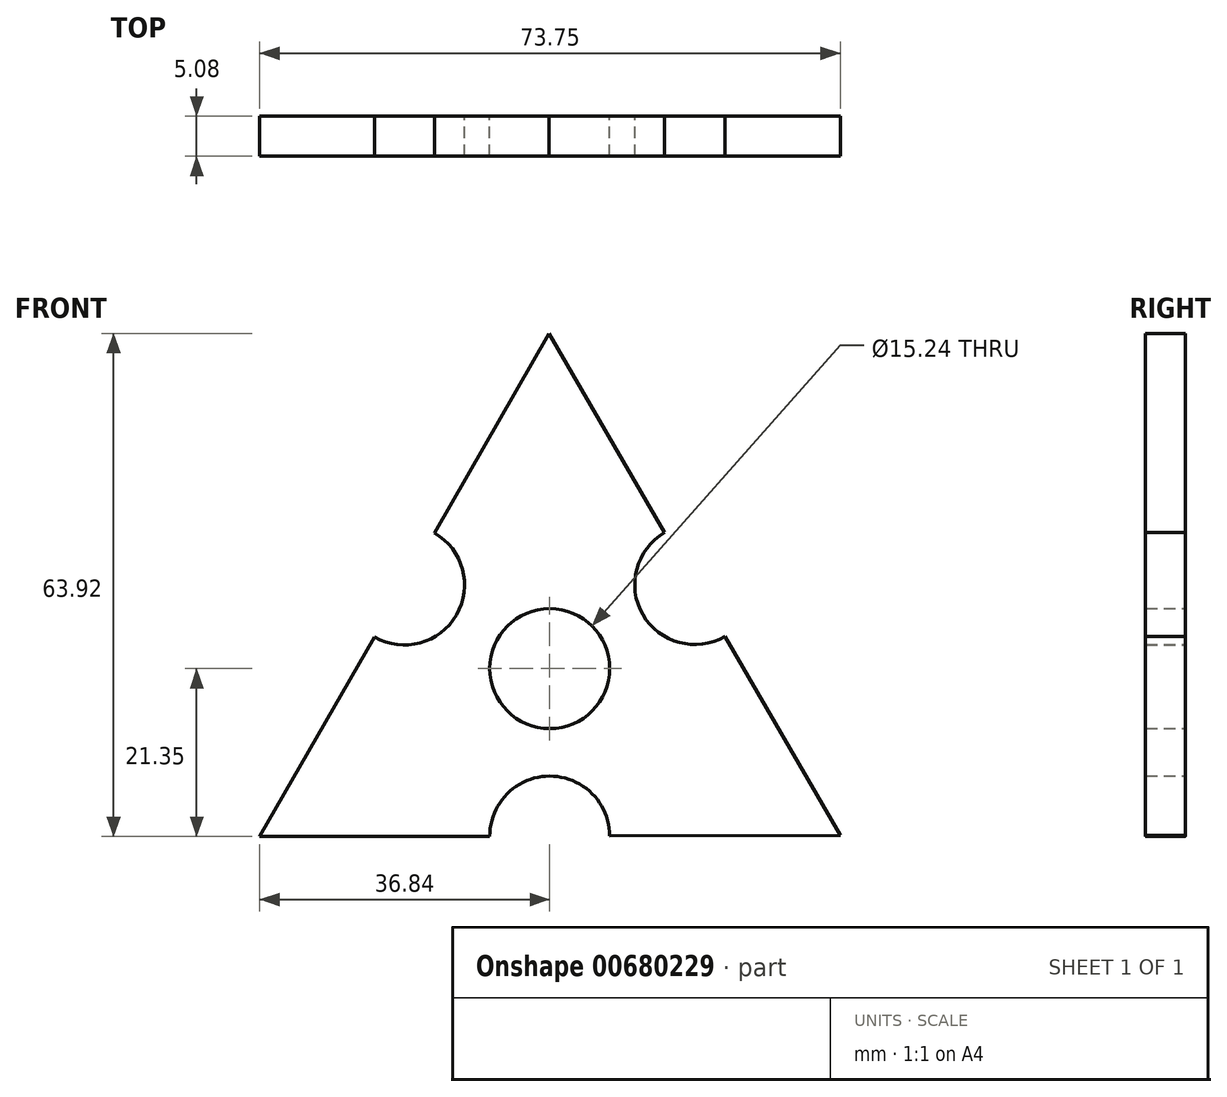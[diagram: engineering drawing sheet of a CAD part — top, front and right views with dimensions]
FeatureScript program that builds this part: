
annotation { "Feature Type Name" : "Feature", "Feature Type Description" : "" }
export const myFeature = defineFeature(function(context is Context, id is Id, definition is map)
    precondition{}
    {
        {
            var Q0;
            Q0=qCreatedBy(makeId("Front.planeOp"),FACE);
            var sketch = newSketch(context, id + "F0", { "sketchPlane" : qUnion([Q0])});
            skCircle(sketch, "E0.cCircle", {"center": v(0, 0) * mm, "radius": 36.87 * mm, "construction": true});
            skLineSegment(sketch, "E0.0", {"start": v(36.9, -21.23) * mm, "end": v(0.07, -42.57) * mm});
            skLineSegment(sketch, "E0.1", {"start": v(0.07, -42.57) * mm, "end": v(-36.84, -21.35) * mm});
            skLineSegment(sketch, "E0.2", {"start": v(-36.84, -21.35) * mm, "end": v(-36.9, 21.23) * mm});
            skLineSegment(sketch, "E0.3", {"start": v(-36.9, 21.23) * mm, "end": v(-0.07, 42.57) * mm});
            skLineSegment(sketch, "E0.4", {"start": v(-0.07, 42.57) * mm, "end": v(36.84, 21.35) * mm});
            skLineSegment(sketch, "E0.5", {"start": v(36.84, 21.35) * mm, "end": v(36.9, -21.23) * mm});
            skPoint(sketch, "E0.0.midPoint", {"position": v(18.49, -31.9) * mm});
            skLineSegment(sketch, "E1", {"start": v(-0.07, 42.57) * mm, "end": v(-36.84, -21.35) * mm});
            skLineSegment(sketch, "E2", {"start": v(-36.84, -21.35) * mm, "end": v(36.9, -21.23) * mm});
            skLineSegment(sketch, "E3", {"start": v(36.9, -21.23) * mm, "end": v(-0.07, 42.57) * mm});
            skCircle(sketch, "E4", {"center": v(-18.45, 10.61) * mm, "radius": 7.62 * mm});
            skCircle(sketch, "E5", {"center": v(18.42, 10.67) * mm, "radius": 7.62 * mm});
            skCircle(sketch, "E6", {"center": v(0, -21.29) * mm, "radius": 7.62 * mm});
            skCircle(sketch, "E7", {"center": v(0, 0) * mm, "radius": 7.62 * mm});
            skSolve(sketch);
        }
        {
            var Q0;
            Q0=makeQuery(id+"F0.imprint","IMPRINT",FACE,{"disambiguationData":[TD([[makeQuery(id+"F0.imprint","IMPRINT",EDGE,{"derivedFrom":sQuery(id+"F0.wireOp",EDGE,"E7")}),-1.0]])]});
            extrude(context, id + "F1", {"entities" : qUnion([Q0]), "depth" : 5.08 * mm, "offsetDistance" : 25.4 * mm});
        }
    });
